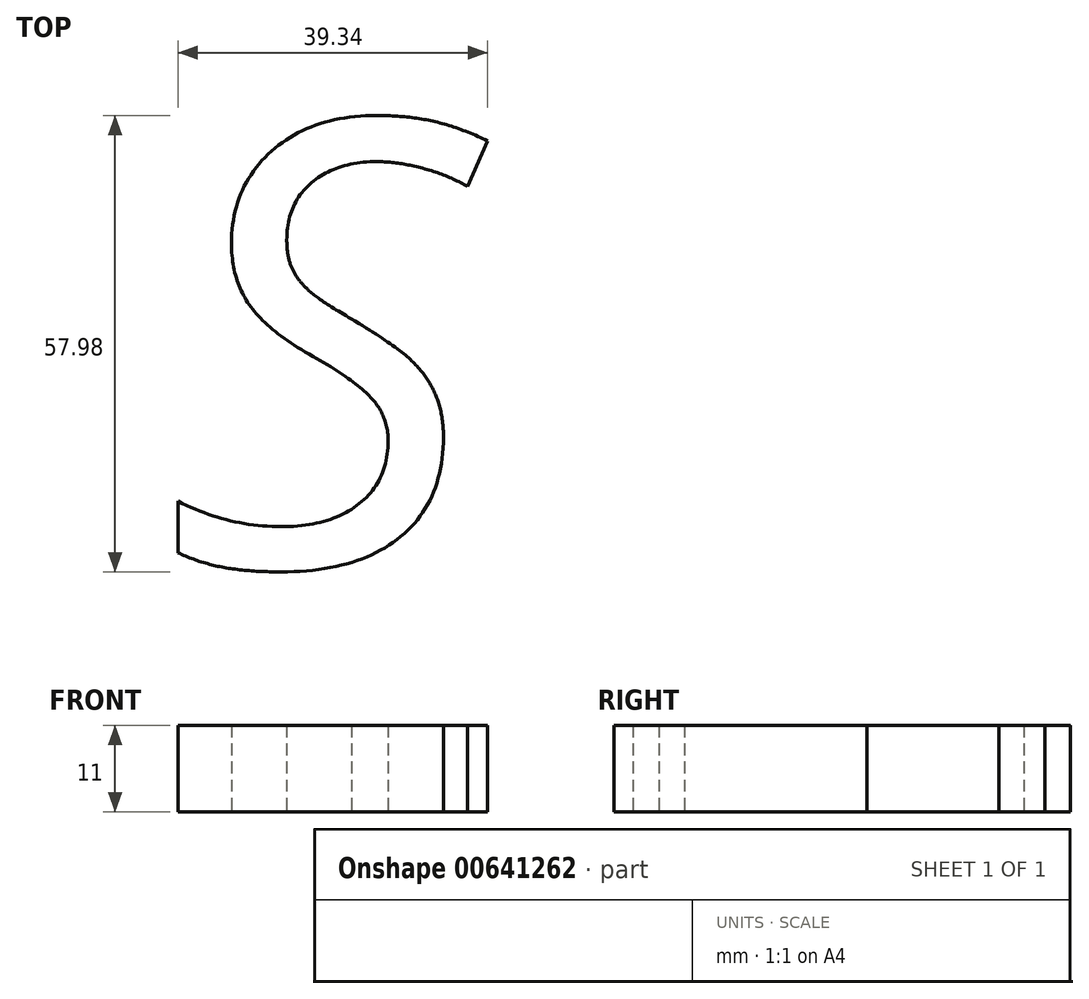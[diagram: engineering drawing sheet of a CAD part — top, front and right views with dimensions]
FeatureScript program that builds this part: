
annotation { "Feature Type Name" : "Feature", "Feature Type Description" : "" }
export const myFeature = defineFeature(function(context is Context, id is Id, definition is map)
    precondition{}
    {
        {
            var Q0;
            Q0=qCreatedBy(makeId("Top.planeOp"),FACE);
            var sketch = newSketch(context, id + "F0", { "sketchPlane" : qUnion([Q0])});
            skText(sketch, "E0", { "text": "S", "fontName": "OpenSans-Italic.ttf"});
            const initialGuessF0  = {"E0": [-0.03124, -0.02844, 1, 0, 0.05688]};
            skSetInitialGuess(sketch, initialGuessF0);
            skSolve(sketch);
        }
        {
            var Q0;
            Q0 = qSketchRegion(id + "F0", true);
            extrude(context, id + "F1", {"entities" : qUnion([Q0]), "depth" : 11 * mm, "offsetDistance" : 25 * mm});
        }
    });
